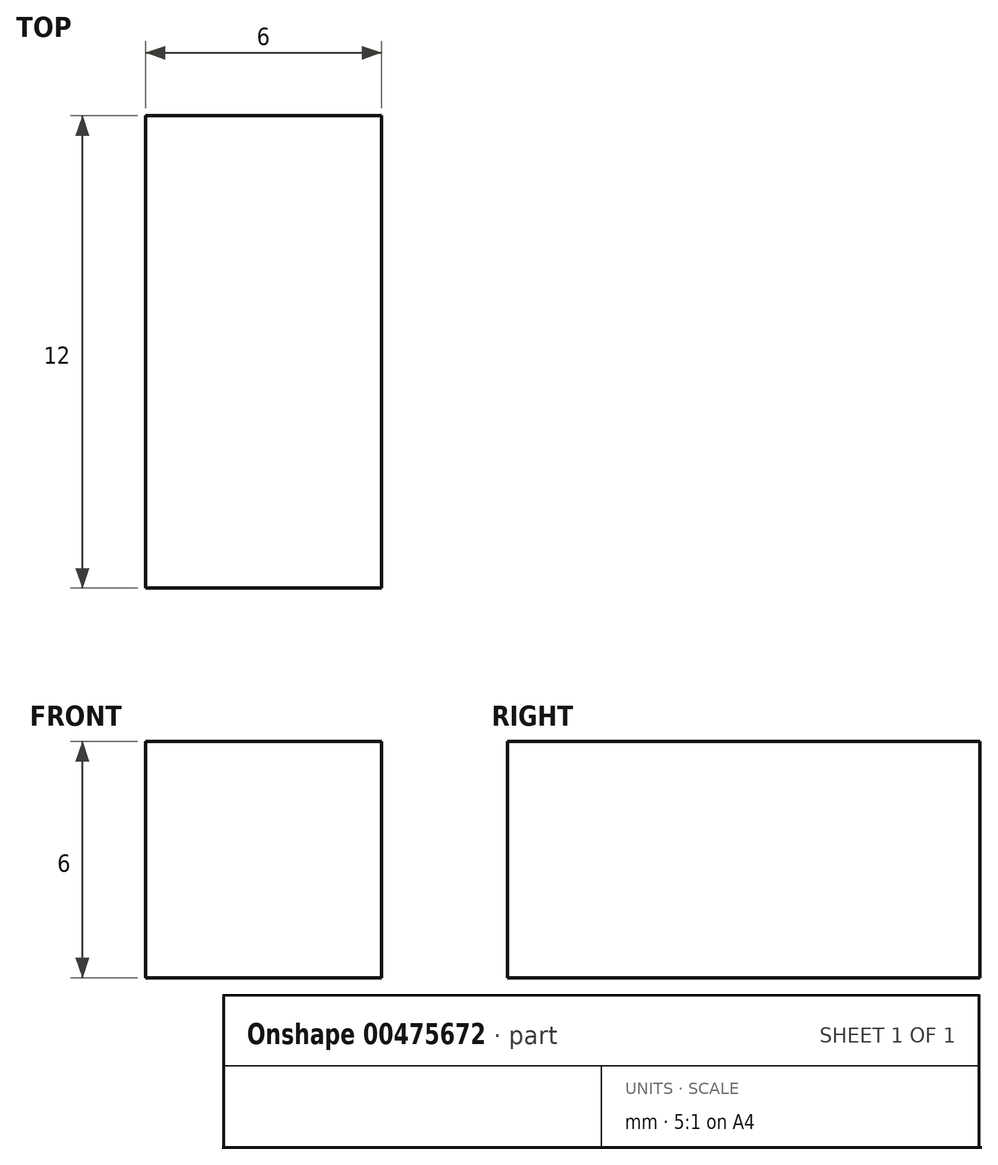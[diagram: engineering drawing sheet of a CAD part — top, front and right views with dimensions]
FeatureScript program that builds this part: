
annotation { "Feature Type Name" : "Feature", "Feature Type Description" : "" }
export const myFeature = defineFeature(function(context is Context, id is Id, definition is map)
    precondition{}
    {
        {
            var Q0;
            Q0=qCreatedBy(makeId("Front.planeOp"),FACE);
            var sketch = newSketch(context, id + "F0", { "sketchPlane" : qUnion([Q0])});
            skLineSegment(sketch, "E0.bottom", {"start": v(0, 0) * mm, "end": v(-3, 0) * mm});
            skLineSegment(sketch, "E0.top", {"start": v(0, 6) * mm, "end": v(-3, 6) * mm});
            skLineSegment(sketch, "E0.right", {"start": v(-3, 0) * mm, "end": v(-3, 6) * mm});
            skLineSegment(sketch, "E1.bottom", {"start": v(0, 0) * mm, "end": v(3, 0) * mm});
            skLineSegment(sketch, "E1.top", {"start": v(0, 6) * mm, "end": v(3, 6) * mm});
            skLineSegment(sketch, "E1.right", {"start": v(3, 0) * mm, "end": v(3, 6) * mm});
            skSolve(sketch);
        }
        {
            var Q0;
            Q0 = qSketchRegion(id + "F0", true);
            extrude(context, id + "F1", {"entities" : qUnion([Q0]), "depth" : 12 * mm});
        }
    });
